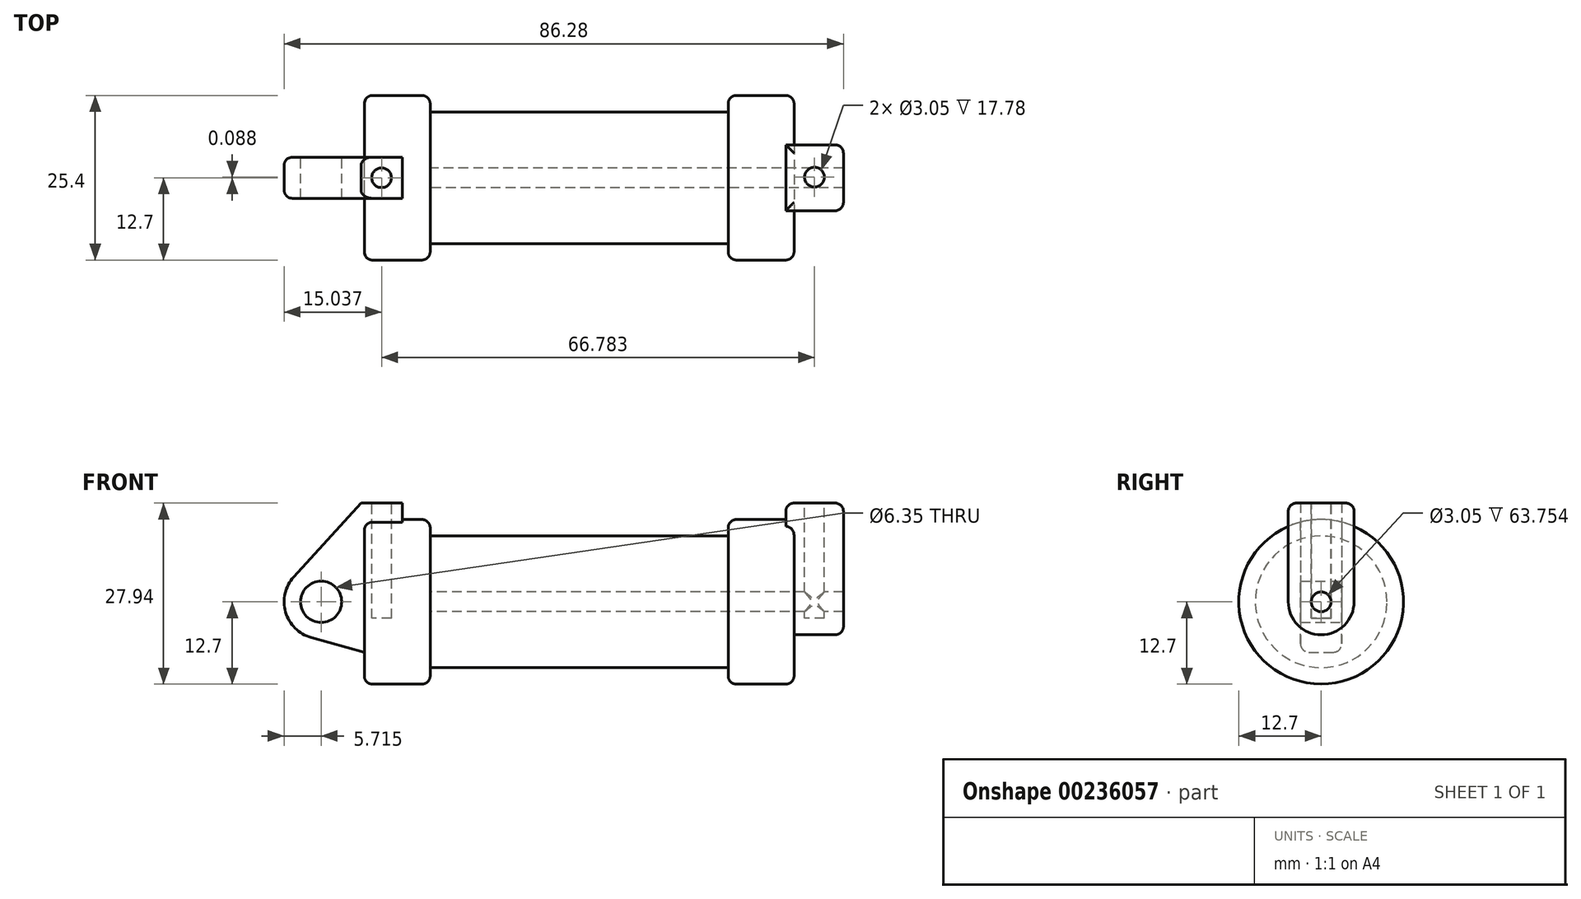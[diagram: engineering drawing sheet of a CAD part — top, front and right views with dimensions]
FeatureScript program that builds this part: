
annotation { "Feature Type Name" : "Feature", "Feature Type Description" : "" }
export const myFeature = defineFeature(function(context is Context, id is Id, definition is map)
    precondition{}
    {
        {
            var Q0;
            Q0=qCreatedBy(makeId("Front.planeOp"),FACE);
            var sketch = newSketch(context, id + "F0", { "sketchPlane" : qUnion([Q0])});
            skLineSegment(sketch, "E0", {"start": v(0, 0) * mm, "end": v(0, 12.7) * mm});
            skLineSegment(sketch, "E1", {"start": v(0, 12.7) * mm, "end": v(10.16, 12.7) * mm});
            skLineSegment(sketch, "E2", {"start": v(10.16, 12.7) * mm, "end": v(10.16, 10.16) * mm});
            skLineSegment(sketch, "E3", {"start": v(10.16, 10.16) * mm, "end": v(56.13, 10.16) * mm});
            skLineSegment(sketch, "E4", {"start": v(56.13, 10.16) * mm, "end": v(56.13, 12.7) * mm});
            skLineSegment(sketch, "E5", {"start": v(56.13, 12.7) * mm, "end": v(66.3, 12.7) * mm});
            skLineSegment(sketch, "E6", {"start": v(66.3, 12.7) * mm, "end": v(66.3, 0) * mm});
            skLineSegment(sketch, "E7", {"start": v(66.3, 0) * mm, "end": v(0, 0) * mm});
            skLineSegment(sketch, "E8", {"start": v(5.84, 15.24) * mm, "end": v(-0.5, 15.24) * mm});
            skLineSegment(sketch, "E9", {"start": v(-0.5, 15.24) * mm, "end": v(-10.88, 3.85) * mm});
            skLineSegment(sketch, "E10", {"start": v(0, 0) * mm, "end": v(-6.65, 0) * mm});
            skCircle(sketch, "E11", {"center": v(-6.65, 0) * mm, "radius": 5.72 * mm});
            skCircle(sketch, "E12", {"center": v(-6.65, 0) * mm, "radius": 3.18 * mm});
            skLineSegment(sketch, "E13", {"start": v(5.84, 15.24) * mm, "end": v(5.84, -9.4) * mm});
            skLineSegment(sketch, "E14", {"start": v(5.84, -9.4) * mm, "end": v(-8.18, -5.5) * mm});
            skSolve(sketch);
        }
        {
            var Q0;
            {var subQ0=sQuery(id+"F0.wireOp",EDGE,"E2");Q0=makeQuery(id+"F0.imprint","IMPRINT",FACE,{"disambiguationData":[TD([[makeQuery(id+"F0.imprint","IMPRINT",EDGE,{"derivedFrom":subQ0}),-1.0]])]});}
            var Q1;
            {var subQ0=sQuery(id+"F0.wireOp",EDGE,"E0");Q1=makeQuery(id+"F0.imprint","IMPRINT",FACE,{"disambiguationData":[TD([[makeQuery(id+"F0.imprint","IMPRINT",EDGE,{"derivedFrom":subQ0}),-1.0]])]});}
            var Q2;
            Q2=sQuery(id+"F0.wireOp",EDGE,"E7");
            revolve(context, id + "F1", {"entities" : qUnion([Q0, Q1]), "axis" : qUnion([Q2]), "revolveType" : RevolveType.FULL});
        }
        {
            var Q0;
            {var subQ3=sQuery(id+"F0.wireOp",EDGE,"E0");Q0=makeQuery(id+"F0.imprint","IMPRINT",FACE,{"disambiguationData":[TD([[makeQuery(id+"F0.imprint","IMPRINT",EDGE,{"derivedFrom":subQ3}),1.0]])]});}
            var Q1;
            {var subQ4=sQuery(id+"F0.wireOp",EDGE,"E12");Q1=makeQuery(id+"F0.imprint","IMPRINT",FACE,{"disambiguationData":[TD([[makeQuery(id+"F0.imprint","IMPRINT",EDGE,{"derivedFrom":subQ4}),-1.0]])]});}
            var Q2;
            {var subQ0=sQuery(id+"F0.wireOp",EDGE,"E14");Q2=makeQuery(id+"F0.imprint","IMPRINT",FACE,{"disambiguationData":[TD([[makeQuery(id+"F0.imprint","IMPRINT",EDGE,{"derivedFrom":subQ0}),-1.0]])]});}
            var Q3;
            {var subQ0=sQuery(id+"F0.wireOp",EDGE,"E0");Q3=makeQuery(id+"F0.imprint","IMPRINT",FACE,{"disambiguationData":[TD([[makeQuery(id+"F0.imprint","IMPRINT",EDGE,{"derivedFrom":subQ0}),-1.0]])]});}
            extrude(context, id + "F2", {"entities" : qUnion([Q0, Q1, Q2, Q3]), "operationType" : NewBodyOperationType.ADD, "endBound" : BoundingType.SYMMETRIC, "depth" : 6.35 * mm});
        }
        {
            var Q0;
            Q0=makeQuery(id+"F1.opRevolve","SWEPT_FACE",FACE,{"disambiguationData":[OSD([sQuery(id+"F0.wireOp",EDGE,"E6")])]});
            var sketch = newSketch(context, id + "F3", { "sketchPlane" : qUnion([Q0])});
            skCircle(sketch, "E15", {"center": v(0, 0) * mm, "radius": 1.52 * mm});
            skCircle(sketch, "E16", {"center": v(0, 0) * mm, "radius": 5.08 * mm});
            skLineSegment(sketch, "E17", {"start": v(5.08, 0) * mm, "end": v(5.08, 15.24) * mm});
            skLineSegment(sketch, "E18", {"start": v(-5.08, 0) * mm, "end": v(-5.08, 15.24) * mm});
            skLineSegment(sketch, "E19", {"start": v(-5.08, 15.24) * mm, "end": v(5.08, 15.24) * mm});
            skSolve(sketch);
        }
        {
            var Q0;
            {var subQ0=sQuery(id+"F3.wireOp",EDGE,"E17");var subQ1=sQuery(id+"F3.wireOp",EDGE,"E16");var subQ2=makeQuery(id+"F3.imprint","INTERSECT",VERTEX,{"derivedFrom":[subQ1,subQ0]});Q0=makeQuery(id+"F3.imprint","IMPRINT",FACE,{"disambiguationData":[TD([[makeQuery(id+"F3.imprint","IMPRINT",EDGE,{"disambiguationData":[TD([[subQ2,-1.0]])],"derivedFrom":subQ1}),-1.0]])]});}
            var Q1;
            Q1=makeQuery(id+"F3.imprint","IMPRINT",FACE,{"disambiguationData":[TD([[makeQuery(id+"F3.imprint","IMPRINT",EDGE,{"derivedFrom":sQuery(id+"F3.wireOp",EDGE,"E15")}),-1.0]])]});
            var Q2;
            {var subQ0=sQuery(id+"F3.wireOp",EDGE,"E19");Q2=makeQuery(id+"F3.imprint","IMPRINT",FACE,{"disambiguationData":[TD([[makeQuery(id+"F3.imprint","IMPRINT",EDGE,{"derivedFrom":subQ0}),-1.0]])]});}
            extrude(context, id + "F4", {"entities" : qUnion([Q0, Q1, Q2]), "operationType" : NewBodyOperationType.ADD, "depth" : 7.62 * mm, "hasSecondDirection" : true, "secondDirectionOppositeDirection" : true, "secondDirectionDepth" : 1.27 * mm});
        }
        {
            var Q0;
            Q0=makeQuery(id+"F2.opExtrude","SWEPT_FACE",FACE,{"disambiguationData":[OSD([sQuery(id+"F0.wireOp",EDGE,"E8")])]});
            var sketch = newSketch(context, id + "F5", { "sketchPlane" : qUnion([Q0])});
            skCircle(sketch, "E20", {"center": v(2.67, 0) * mm, "radius": 1.52 * mm});
            skPoint(sketch, "E20.centerSnap0", {"position": v(2.67, 3.18) * mm});
            skPoint(sketch, "E20.centerSnap1", {"position": v(-0.5, 0) * mm});
            skCircle(sketch, "E21", {"center": v(69.45, 0.09) * mm, "radius": 1.52 * mm});
            skSolve(sketch);
        }
        {
            var Q0;
            Q0=makeQuery(id+"F4.boolean.opBoolean","SPLIT",FACE,{"disambiguationData":[TD([makeQuery(id+"F4.opExtrude","SWEPT_FACE",FACE,{"disambiguationData":[OSD([sQuery(id+"F3.wireOp",EDGE,"E15")])]})])],"derivedFrom":makeQuery(id+"F1.opRevolve","SWEPT_FACE",FACE,{"disambiguationData":[OSD([sQuery(id+"F0.wireOp",EDGE,"E6")])]})});
            var Q1;
            Q1=makeQuery(id+"F1.opRevolve","SWEPT_FACE",FACE,{"disambiguationData":[OSD([sQuery(id+"F0.wireOp",EDGE,"E2")])]});
            extrude(context, id + "F6", {"entities" : qUnion([Q0]), "operationType" : NewBodyOperationType.REMOVE, "endBound" : BoundingType.UP_TO_SURFACE, "oppositeDirection" : true, "endBoundEntityFace" : qUnion([Q1]), "depth" : 25.4 * mm});
        }
        {
            var Q0;
            Q0=makeQuery(id+"F5.imprint","IMPRINT",FACE,{"disambiguationData":[TD([[makeQuery(id+"F5.imprint","IMPRINT",EDGE,{"derivedFrom":sQuery(id+"F5.wireOp",EDGE,"E20")}),1.0]])]});
            var Q1;
            Q1=makeQuery(id+"F5.imprint","IMPRINT",FACE,{"disambiguationData":[TD([[makeQuery(id+"F5.imprint","IMPRINT",EDGE,{"derivedFrom":sQuery(id+"F5.wireOp",EDGE,"E21")}),1.0]])]});
            extrude(context, id + "F7", {"entities" : qUnion([Q0, Q1]), "operationType" : NewBodyOperationType.REMOVE, "oppositeDirection" : true, "depth" : 17.78 * mm});
        }
        {
            var Q0;
            Q0=makeQuery(id+"F1.opRevolve","SWEPT_EDGE",EDGE,{"disambiguationData":[OSD([sQuery(id+"F0.wireOp",EDGE,"E1"),sQuery(id+"F0.wireOp",EDGE,"E2")])]});
            var Q1;
            Q1=makeQuery(id+"F1.opRevolve","SWEPT_EDGE",EDGE,{"disambiguationData":[OSD([sQuery(id+"F0.wireOp",EDGE,"E4"),sQuery(id+"F0.wireOp",EDGE,"E5")])]});
            var Q2;
            Q2=makeQuery(id+"F1.opRevolve","SWEPT_EDGE",EDGE,{"disambiguationData":[OSD([sQuery(id+"F0.wireOp",EDGE,"E0"),sQuery(id+"F0.wireOp",EDGE,"E1")])]});
            var Q3;
            Q3=makeQuery(id+"F1.opRevolve","SWEPT_EDGE",EDGE,{"disambiguationData":[OSD([sQuery(id+"F0.wireOp",EDGE,"E5"),sQuery(id+"F0.wireOp",EDGE,"E6")])]});
            var Q4;
            Q4=makeQuery(id+"F2.opExtrude","CAP_EDGE",EDGE,{"disambiguationData":[OSD([sQuery(id+"F0.wireOp",EDGE,"E9")])],"isStart":false});
            var Q5;
            Q5=makeQuery(id+"F2.opExtrude","CAP_EDGE",EDGE,{"disambiguationData":[OSD([sQuery(id+"F0.wireOp",EDGE,"E9")])],"isStart":true});
            var Q6;
            Q6=makeQuery(id+"F2.opExtrude","CAP_EDGE",EDGE,{"disambiguationData":[OSD([sQuery(id+"F0.wireOp",EDGE,"E14")])],"isStart":true});
            var Q7;
            Q7=makeQuery(id+"F2.opExtrude","CAP_EDGE",EDGE,{"disambiguationData":[OSD([sQuery(id+"F0.wireOp",EDGE,"E14")])],"isStart":false});
            var Q8;
            Q8=makeQuery(id+"F4.opExtrude","SWEPT_EDGE",EDGE,{"disambiguationData":[OSD([sQuery(id+"F3.wireOp",EDGE,"E17"),sQuery(id+"F3.wireOp",EDGE,"E19")])]});
            var Q9;
            Q9=makeQuery(id+"F4.opExtrude","CAP_EDGE",EDGE,{"disambiguationData":[OSD([sQuery(id+"F3.wireOp",EDGE,"E19")])],"isStart":false});
            var Q10;
            Q10=makeQuery(id+"F4.opExtrude","SWEPT_EDGE",EDGE,{"disambiguationData":[OSD([sQuery(id+"F3.wireOp",EDGE,"E18"),sQuery(id+"F3.wireOp",EDGE,"E19")])]});
            var Q11;
            Q11=makeQuery(id+"F4.opExtrude","CAP_EDGE",EDGE,{"disambiguationData":[OSD([sQuery(id+"F3.wireOp",EDGE,"E19")])],"isStart":true});
            var Q12;
            Q12=makeQuery(id+"F4.opExtrude","CAP_EDGE",EDGE,{"disambiguationData":[OSD([sQuery(id+"F3.wireOp",EDGE,"E18")])],"isStart":false});
            var Q13;
            Q13=makeQuery(id+"F4.opExtrude","CAP_EDGE",EDGE,{"disambiguationData":[OSD([sQuery(id+"F3.wireOp",EDGE,"E17")])],"isStart":false});
            fillet(context, id + "F8", {"entities" : qUnion([Q0, Q1, Q2, Q3, Q4, Q5, Q6, Q7, Q8, Q9, Q10, Q11, Q12, Q13]), "radius" : 1.27 * mm, "tangentPropagation" : true, "allowEdgeOverflow" : false});
        }
    });
